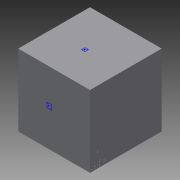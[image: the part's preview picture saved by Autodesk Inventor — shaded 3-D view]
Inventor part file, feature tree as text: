
AUTODESK INVENTOR PART (.ipt)
format: ipt  version: 2014 (Build 180170000, 170)  size: 624,128 bytes
history: native  units: mm
features: sketch x56, extrude x53, other x51
ambient origin geometry x8: Origin, YZ Plane, XZ Plane, XY Plane, X Axis, Y Axis, Z Axis, Center Point
bodies: 实体1 (feature_tree)
feature tree (160):
  extrude  "拉伸1"  Depth=200.0mm
  other  "UCS1"
  other  "UCS2"
  other  "UCS3"
  other  "UCS4"
  other  "UCS5"
  other  "UCS6"
  extrude  "拉伸2"  Depth=43.0mm
  extrude  "拉伸3"  Depth=4.25mm
  extrude  "拉伸4"  Depth=15.5mm
  extrude  "拉伸5"  TaperAngle=0.0deg  [1 undecoded]
  extrude  "拉伸6"  Depth=0.75mm
  extrude  "拉伸7"  Depth=31.75mm
  extrude  "拉伸8"  Depth=18.5mm
  extrude  "拉伸9"  Depth=18.5mm
  extrude  "拉伸10"  Depth=5.0mm
  extrude  "拉伸11"  Depth=16.0mm
  extrude  "拉伸12"  Depth=21.5mm
  extrude  "拉伸13"  Depth=12.7mm
  extrude  "拉伸14"  Depth=21.5mm
  other  "iFeature2:1"
  other  "Footprint1"
  other  "Footprint4"
  extrude  "拉伸15"  Depth=30.2mm
  extrude  "拉伸20"  Depth=21.0mm
  extrude  "拉伸21"  Depth=21.0mm
  extrude  "拉伸22"  Depth=4.0mm
  extrude  "拉伸23"  Depth=33.0mm
  extrude  "拉伸24"  Depth=4.0mm
  extrude  "拉伸25"  TaperAngle=0.0deg  [1 undecoded]
  extrude  "拉伸26"  TaperAngle=0.0deg  [1 undecoded]
  extrude  "拉伸27"  Depth=30.0mm
  extrude  "拉伸28"  Depth=12.0mm
  extrude  "拉伸29"  Depth=10.25mm
  extrude  "拉伸30"  Depth=35.05mm
  extrude  "拉伸31"  Depth=95.0mm
  extrude  "拉伸32"  Depth=50.0mm
  extrude  "拉伸33"  Depth=6.8mm
  extrude  "拉伸36"  Depth=38.1mm
  extrude  "拉伸37"  TaperAngle=0.0deg  [1 undecoded]
  extrude  "拉伸38"  Depth=76.2mm
  extrude  "拉伸39"  Depth=82.6mm
  extrude  "拉伸40"  Depth=26.0mm
  extrude  "拉伸41"  Depth=26.0mm
  extrude  "拉伸42"  Depth=8.0mm
  extrude  "拉伸43"  Depth=22.0mm
  extrude  "拉伸44"  Depth=9.5mm
  extrude  "拉伸45"  Depth=28.0mm
  extrude  "拉伸46"  Depth=12.0mm
  extrude  "拉伸47"  Depth=29.0mm TaperAngle=0.0deg
  extrude  "拉伸48"  Depth=11.1mm
  extrude  "拉伸49"  Depth=38.0mm
  extrude  "拉伸50"  Depth=14.7mm
  extrude  "拉伸51"  Depth=73.8mm
  extrude  "拉伸52"  Depth=31.0mm
  extrude  "拉伸53"  Depth=57.0mm
  extrude  "拉伸54"  Depth=32.0mm TaperAngle=0.0deg
  extrude  "拉伸55"  Depth=7.5mm
  extrude  "拉伸56"  Depth=4.0mm
  extrude  "拉伸57"  Depth=4.0mm
  extrude  "拉伸58"  Depth=4.0mm
  extrude  "拉伸59"  Depth=8.0mm TaperAngle=0.0deg
  sketch  "草图1"  dims[d0=1000.0mm d1=0.0mm]
  sketch  "草图2"  dims[d2=0.0mm d3=0.0mm d4=0.0mm d5=0.0mm d6=0.0mm d7=0.0mm]
  sketch  "草图3"  dims[d8=0.0mm d9=0.0mm d10=0.0mm d11=0.0mm d12=0.0mm d13=0.0mm]
  sketch  "草图4"  dims[d14=0.0mm d15=0.0mm d16=0.0mm d17=0.0mm d18=0.0mm d19=0.0mm]
  sketch  "草图5"  dims[d20=0.0mm d21=0.0mm d22=0.0mm d23=0.0mm d24=0.0mm d25=0.0mm]
  sketch  "草图6"  dims[d26=0.0mm d27=0.0mm d28=0.0mm d29=0.0mm d30=0.0mm d31=0.0mm]
  sketch  "草图7"  dims[d32=0.0mm d33=0.0mm d34=0.0mm d35=0.0mm d36=0.0mm d37=0.0mm d38=200.0mm]
  sketch  "草图8"  dims[d39=100.0mm d40=43.0mm]
  sketch  "草图9"  dims[d41=51.0mm d42=4.25mm]
  sketch  "草图10"  dims[d43=21.5mm d44=15.5mm]
  sketch  "草图11"  dims[d45=31.0mm d46=0.0mm]
  sketch  "草图12"  dims[d47=40.5mm d48=0.75mm]
  sketch  "草图13"  dims[d49=40.5mm d50=31.75mm]
  sketch  "草图14"  dims[d51=18.5mm d52=0.0mm d53=18.5mm d54=-10.297443mm]
  sketch  "草图24"  dims[d67=25.9mm d68=21.5mm]
  sketch  "草图29"  dims[d69=15.5mm d70=12.7mm]
  sketch  "草图30"  dims[d71=5.1mm d72=21.5mm]
  sketch  "草图31"  dims[d73=15.5mm d74=30.2mm]
  sketch  "草图32"  dims[d75=21.0mm d76=0.0mm d77=21.0mm d78=-10.297443mm]
  sketch  "草图33"  dims[d79=21.0mm d80=-10.297443mm d81=21.0mm d82=-10.297443mm]
  sketch  "草图34"  dims[d83=21.0mm d84=-10.297443mm d85=4.0mm]
  sketch  "草图35"  dims[d86=31.75mm d87=33.0mm]
  sketch  "草图36"  dims[d88=4.0mm d89=0.0mm d90=4.0mm d91=-10.297443mm]
  sketch  "草图37"  dims[d105=0.0mm d119=0.0mm]
  sketch  "草图38"  dims[d125=0.0mm d131=0.0mm]
  sketch  "草图39"  dims[d135=0.0mm d139=30.0mm]
  sketch  "草图40"  dims[d140=20.0mm d141=12.0mm]
  sketch  "草图41"  dims[d142=19.05mm d143=0.0mm d153=10.25mm]
  sketch  "草图42"  dims[d154=35.05mm d155=0.0mm d156=35.05mm d157=-10.297443mm]
  sketch  "草图45"  dims[d158=35.05mm d159=-10.297443mm d160=95.0mm]
  sketch  "草图46"  dims[d161=102.0mm d162=50.0mm]
  sketch  "草图47"  dims[d163=100.0mm d167=6.8mm]
  sketch  "草图48"  dims[d168=41.8mm d169=38.1mm]
  sketch  "草图49"  dims[d170=76.2mm d171=0.0mm]
  sketch  "草图50"  dims[d172=82.6mm d173=76.2mm]
  sketch  "草图51"  dims[d174=0.0mm d175=82.6mm]
  sketch  "草图52"  dims[d176=26.0mm d177=0.0mm d178=26.0mm d179=-10.297443mm]
  sketch  "草图55"  dims[d180=26.0mm d181=-10.297443mm d182=26.0mm d183=-10.297443mm]
  sketch  "草图56"  dims[d184=26.0mm d185=-10.297443mm d186=8.0mm]
  sketch  "草图57"  dims[d187=22.0mm d188=0.0mm d189=14.7mm]
  sketch  "草图58"  dims[d190=38.0mm d191=9.5mm]
  sketch  "草图59"  dims[d204=28.0mm d205=0.0mm d206=28.0mm d207=-10.297443mm]
  sketch  "草图60"  dims[d208=6.3mm d209=12.0mm]
  sketch  "草图61"  dims[d210=11.8mm d211=29.0mm d212=0.0mm]
  sketch  "草图62"  dims[d213=29.0mm d214=-10.297443mm d215=11.1mm]
  sketch  "草图63"  dims[d216=46.8mm d217=38.0mm]
  sketch  "草图64"  dims[d218=30.0mm d219=0.0mm d224=14.7mm]
  sketch  "草图65"  dims[d225=19.0mm d226=73.8mm]
  sketch  "草图66"  dims[d227=31.0mm d228=0.0mm d229=31.0mm d230=-10.297443mm]
  sketch  "草图67"  dims[d231=14.7mm d232=57.0mm]
  sketch  "草图68"  dims[d233=73.8mm d234=32.0mm d235=0.0mm]
  sketch  "草图69"  dims[d236=32.0mm d237=-10.297443mm d238=7.5mm]
  sketch  "草图70"  dims[d239=3.2mm d240=23.8mm d241=79.4mm d242=23.8mm d243=8.0mm d244=0.0mm d245=8.0mm d246=-10.297443mm d247=8.0mm d248=-10.297443mm d249=8.0mm d250=-10.297443mm d267=43.0mm d268=51.0mm d269=50.0mm d270=200.0mm d271=21.5mm d272=15.5mm d273=4.25mm d274=0.75mm d275=40.5mm d276=40.5mm d277=31.75mm d278=0.0mm d279=31.0mm d280=18.5mm d281=0.0mm d282=18.5mm d283=-10.297443mm d284=18.5mm d285=-10.297443mm d286=18.5mm d287=-10.297443mm d288=18.5mm d289=-10.297443mm d290=5.0mm d291=16.0mm d292=0.0mm d293=7.5mm d294=21.5mm d295=5.1mm d296=21.0mm d297=0.0mm d298=21.0mm d299=-10.297443mm d300=7.5mm d301=12.7mm d302=15.5mm d303=19.0mm d304=0.0mm d305=19.0mm d306=-10.297443mm d307=7.5mm d308=15.5mm d309=30.2mm d310=20.0mm d311=0.0mm d312=20.0mm d313=-10.297443mm d314=7.5mm d315=25.9mm d316=21.5mm d317=18.0mm d318=0.0mm d319=18.0mm d320=-10.297443mm d321=4.0mm d322=33.0mm d323=31.75mm d324=4.0mm d325=0.0mm d326=4.0mm d327=-10.297443mm]
  other  "UCS1: YZ 平面"
  other  "UCS1: XZ 平面"
  other  "UCS1: XY 平面"
  other  "UCS1: X 轴"
  other  "UCS1: Y 轴"
  other  "UCS1: Z 轴"
  other  "UCS1: 原点"
  other  "UCS2: YZ 平面"
  other  "UCS2: XZ 平面"
  other  "UCS2: XY 平面"
  other  "UCS2: X 轴"
  other  "UCS2: Y 轴"
  other  "UCS2: Z 轴"
  other  "UCS2: 原点"
  other  "UCS3: YZ 平面"
  other  "UCS3: XZ 平面"
  other  "UCS3: XY 平面"
  other  "UCS3: X 轴"
  other  "UCS3: Y 轴"
  other  "UCS3: Z 轴"
  other  "UCS3: 原点"
  other  "UCS4: YZ 平面"
  other  "UCS4: XZ 平面"
  other  "UCS4: XY 平面"
  other  "UCS4: X 轴"
  other  "UCS4: Y 轴"
  other  "UCS4: Z 轴"
  other  "UCS4: 原点"
  other  "UCS5: YZ 平面"
  other  "UCS5: XZ 平面"
  other  "UCS5: XY 平面"
  other  "UCS5: X 轴"
  other  "UCS5: Y 轴"
  other  "UCS5: Z 轴"
  other  "UCS5: 原点"
  other  "UCS6: YZ 平面"
  other  "UCS6: XZ 平面"
  other  "UCS6: XY 平面"
  other  "UCS6: X 轴"
  other  "UCS6: Y 轴"
  other  "UCS6: Z 轴"
  other  "UCS6: 原点"
  sketch  "草图15"  dims[d55=18.5mm d56=-10.297443mm d57=18.5mm d58=-10.297443mm]
  sketch  "草图16"  dims[d59=18.5mm d60=-10.297443mm d61=5.0mm]
  sketch  "草图18"  dims[d62=16.0mm d63=0.0mm d64=7.5mm]
note: 4 required parameter values undecoded (feature->parameter linkage not recoverable at this tier; creation-order binding heuristic only, values carry confidence <= 0.55)
